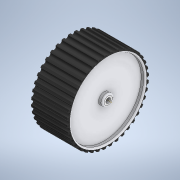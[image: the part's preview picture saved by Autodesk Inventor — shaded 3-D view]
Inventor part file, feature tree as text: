
AUTODESK INVENTOR PART (.ipt)
format: ipt  version: 2020 (Build 240168000, 168)  size: 630,784 bytes
history: native  units: in
note: dims shown in document units (in); Inventor stores cm internally (conversion verified against a paired STEP export)
features: sketch x6, extrude x5, fillet x5, hole x1, other x1
ambient origin geometry x8: Origin, YZ Plane, XZ Plane, XY Plane, X Axis, Y Axis, Z Axis, Center Point
bodies: Solid4 (feature_tree)
feature tree (18):
  extrude  "Extrusion4"  Depth=3.937in
  extrude  "Extrusion5"  Depth=3.7402in
  hole  "Hole2"  [1 undecoded]
  extrude  "Extrusion6"  Depth=3.1496in TaperAngle=360.0deg
  extrude  "Extrusion8"  Depth=0.552in
  extrude  "Extrusion9"  Depth=3.5923in
  fillet  "Fillet1"  Radius=0.1969in
  fillet  "Fillet2"  Radius=0.0787in
  fillet  "Fillet3"  Radius=0.0787in
  fillet  "Fillet4"  Radius=0.0787in
  fillet  "Fillet5"  Radius=0.0787in
  other  "Work Axis1"
  sketch  "Sketch7"  dims[d17=3.7402in d18=3.937in]
  sketch  "Sketch8"  dims[d19=1.7717in d20=0.0in d21=3.7402in]
  sketch  "Sketch9"  dims[d22=1.5748in d23=0.0in]
  sketch  "Sketch10"  dims[d24=0.2362in d25=0.2362in d26=0.1575in d27=0.0787in d28=90.0deg d29=0.315in d30=0.8108in d31=15.748in d33=360.0deg]
  sketch  "Sketch13"  dims[d35=1.7717in d36=0.0in d48=3.1496in d50=360.0deg]
  sketch  "Sketch14"  dims[d52=0.5906in d53=0.0in d54=0.552in d55=3.5923in d56=0.1969in d57=0.0in d58=0.0787in d59=0.0787in d60=0.0787in d61=0.0787in d62=0.0787in d32=0.8108in d34=0.0295in d37=0.0197in d38=0.0344in]
note: 1 required parameter value undecoded (feature->parameter linkage not recoverable at this tier; creation-order binding heuristic only, values carry confidence <= 0.55)
